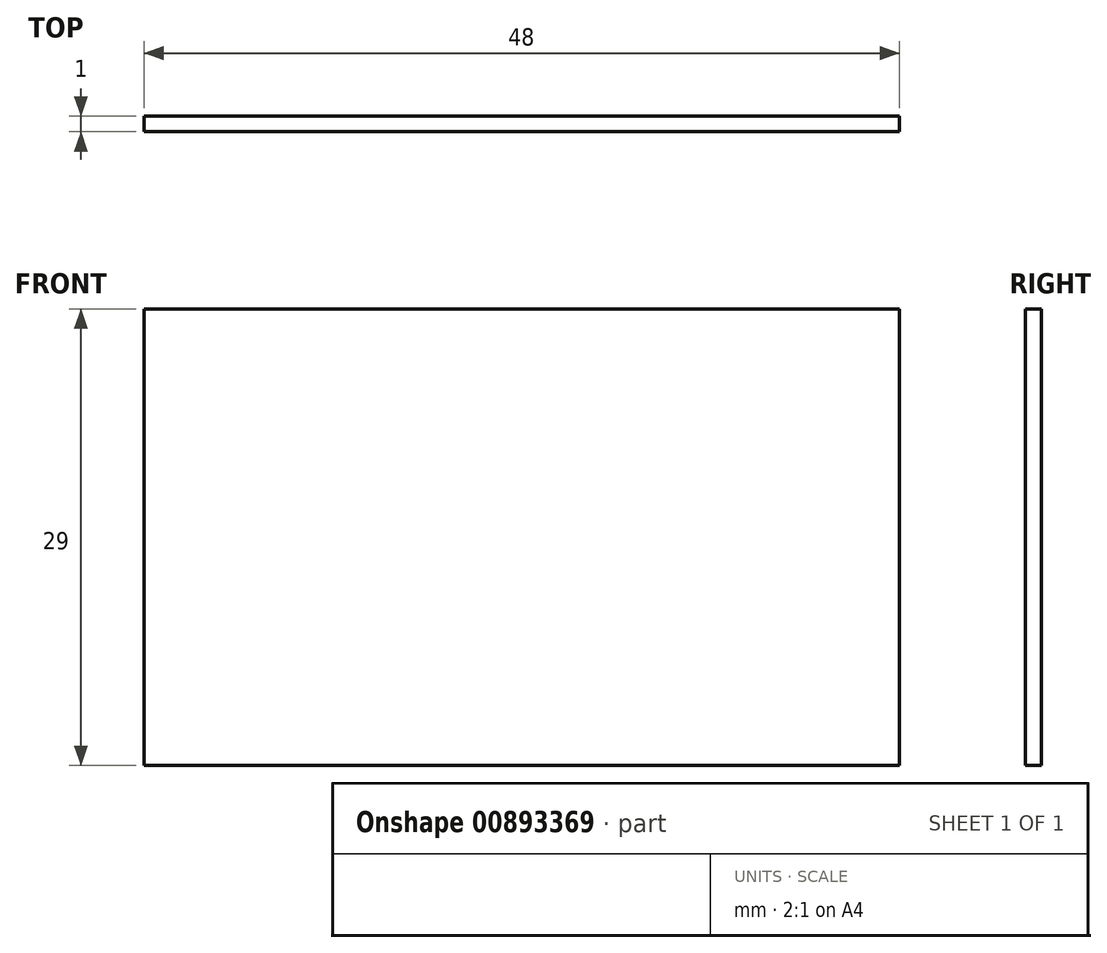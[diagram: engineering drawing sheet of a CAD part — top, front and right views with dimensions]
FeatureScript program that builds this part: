
annotation { "Feature Type Name" : "Feature", "Feature Type Description" : "" }
export const myFeature = defineFeature(function(context is Context, id is Id, definition is map)
    precondition{}
    {
        {
            var Q0;
            Q0=qCreatedBy(makeId("Front.planeOp"),FACE);
            var sketch = newSketch(context, id + "F0", { "sketchPlane" : qUnion([Q0])});
            skLineSegment(sketch, "E0.bottom", {"start": v(24, 14.5) * mm, "end": v(-24, 14.5) * mm});
            skLineSegment(sketch, "E0.top", {"start": v(24, -14.5) * mm, "end": v(-24, -14.5) * mm});
            skLineSegment(sketch, "E0.left", {"start": v(24, 14.5) * mm, "end": v(24, -14.5) * mm});
            skLineSegment(sketch, "E0.right", {"start": v(-24, 14.5) * mm, "end": v(-24, -14.5) * mm});
            skPoint(sketch, "E0.middle", {"position": v(0, 0) * mm});
            skSolve(sketch);
        }
        {
            var Q0;
            Q0=makeQuery(id+"F0.imprint","IMPRINT",FACE,{"disambiguationData":[TD([[makeQuery(id+"F0.imprint","IMPRINT",EDGE,{"derivedFrom":sQuery(id+"F0.wireOp",EDGE,"E0.bottom")}),1.0]])]});
            extrude(context, id + "F1", {"entities" : qUnion([Q0]), "depth" : 1 * mm, "offsetDistance" : 25 * mm});
        }
    });
